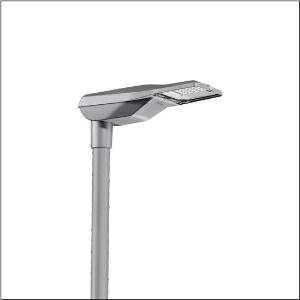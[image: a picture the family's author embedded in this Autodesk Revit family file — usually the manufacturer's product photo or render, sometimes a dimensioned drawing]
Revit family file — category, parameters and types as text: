
# Revit family: streetlight_sl_21_iq_micro___st1_5a_5xe1p41g08db_1f20
name_source: partatom
category: Lighting Fixtures
units: mm (PartAtom-declared; Revit-internal decimal feet)

## family parameters
Cut with Voids When Loaded = No
Host = Face
Light Source = No
Part Type = Normal
Room Calculation Point = No
Round Connector Dimension = Use Diameter
Shared = No

## types (1)
- --- (1 x LED, 4930 lm, 36.4 W, 4000K)
    Apparent Load = 36 VA
    CIE Flux Codes = 22 53 95 100 100
    Color Rendering = 70
    Color Temperature = 4000K
    Default Elevation = 1800 mm
    Description = Streetlight SL 21 iQ micro, mast luminaire, primary light control with lens, of PMMA, primary optical cover: cover, of toughened safety glass, transparent, light distribution: ST1.5a, light emission: direct distribution, primary light characteristic: asymmetric, installation type: post-top, side-entry, LED, High Power LED, rated luminous flux: 4.930lm, luminous efficacy: 135lm/W, light colour: 740, colour temperature: 4000K, control: Street-Remote, Auto-Match, Temp-Guard, Lumen-Switch, Night-Set, Smart-Wire, Light-Fading, Desk-Remote (wireless, voltage-free reading and setting of iQ features in the workshop via application-optimized NFC function/RFID function), optimised constant luminous flux control (CLO 2.0), presetting dimming linear, mains connection: 220..240V, AC, 50/60Hz, start of lifetime: 36W, end of service life: 38W, reduction: 16W, luminaire housing, of diecast aluminium, powder-coated, Siteco® metallic grey (DB 702S), corrosivity category C5 mid according to DIN EN ISO 12944, please order mast flange separately, inclination adjustable: 0°, 5°, 10°, 15°, sealing non-destructively replaceable, multi-level sealing system, length: 528mm, width: 235mm, height: 110mm, mast flange for spigot size: 42mm (side-entry): 5XC10008XM4, 60/48mm (side-entry/post-top): 5XC10108XM2, 76/60mm (side-entry/post-top): 5XC10108XM1, protection rating (complete): IP66, insulation class (complete): insulation class II (safety insulation), certification: CE, ENEC, ENEC+, VDE, impact resistance: IK09, permissible operating ambient temperature for outdoor applications: -40..+50°C, standard-compliant lighting for roads and squares, packaging unit: 1 piece

Light Distribution: ST1.5a
    Height = 110 mm
    Lamp = 1 x LED
    Lamp Light Flux = 4930 lm
    Lamp Power = 36.4 W
    Lamp count = 1
    Length = 528 mm
    Luminous efficacy = 135 lm/W
    Manufacturer = Siteco
    ModVariant = No
    Model = 5XE1P41G08DB
    Number of Poles = 1
    OnlyDefault = Yes
    Power Factor = 1
    Product Name = Streetlight SL 21 iQ micro | ST1.5a
    Product group = mast luminaire | pylon top
    ProductGroupID = 6100
    Protection Class = Protection class II
    Protection Degree = IP 66
    RLX_Detail_Level = 1
    RLX_Emergency_Light_Flux = 0 lm
    RLX_Emergency_Type = 0
    RLX_Emergency_Type_DB = No
    RlxData = <blob elided: 102961 chars, md5=9133f6e0>
    Socket = socket
    Standby Power = 0 W
    System Light Flux = 4930 lm
    System Power = 36 W
    Type Comments = factory setting: luminous flux: 100 % | dim-lin: 254 | 715 mA
    Type Image = l_1006881.jpg
    URL = http://relux.com
    VarID = @adj_086091
    Voltage = 0 V
    Weight = 0.00 kg
    Width = 235 mm

## geometry (parser evidence)
native form markers: Blend x4, Sweep x12
no freeform markers — native parametric forms only
